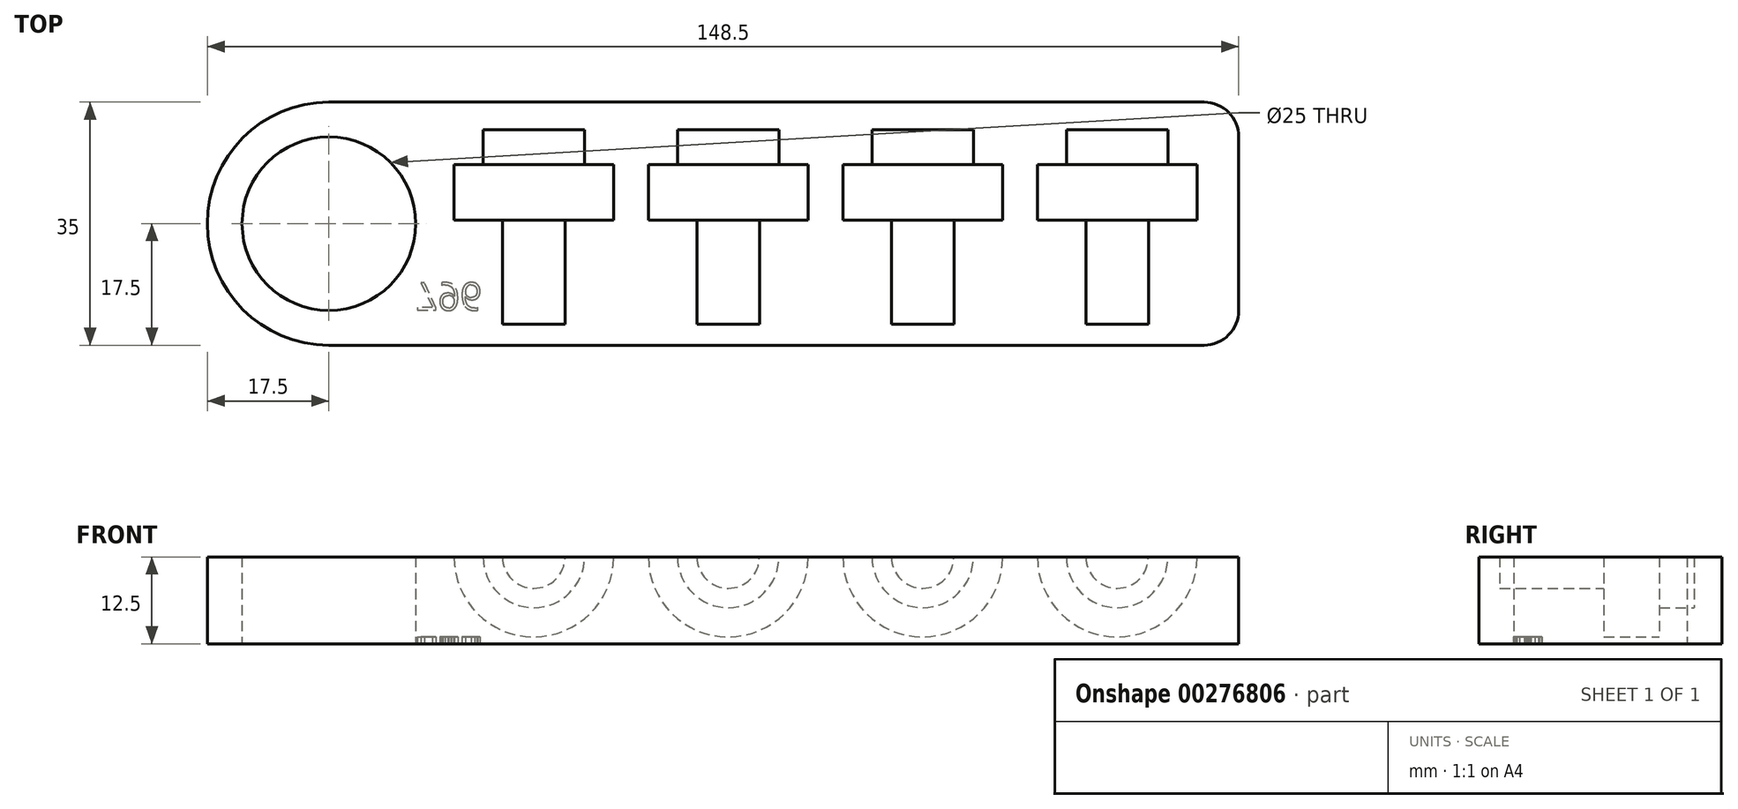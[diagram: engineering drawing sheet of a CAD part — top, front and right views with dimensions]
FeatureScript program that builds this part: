
annotation { "Feature Type Name" : "Feature", "Feature Type Description" : "" }
export const myFeature = defineFeature(function(context is Context, id is Id, definition is map)
    precondition{}
    {
        {
            var Q0;
            Q0=qCreatedBy(makeId("Top.planeOp"),FACE);
            var sketch = newSketch(context, id + "F0", { "sketchPlane" : qUnion([Q0])});
            skLineSegment(sketch, "E0.bottom", {"start": v(17.5, 0) * mm, "end": v(143.5, 0) * mm});
            skLineSegment(sketch, "E0.top", {"start": v(17.5, 35) * mm, "end": v(143.5, 35) * mm});
            skLineSegment(sketch, "E0.left", {"start": v(0, 17.5) * mm, "end": v(0, 17.5) * mm});
            skLineSegment(sketch, "E0.right", {"start": v(148.5, 5) * mm, "end": v(148.5, 30) * mm});
            skLineSegment(sketch, "E1.bottom", {"start": v(0, 0) * mm, "end": v(17.5, 0) * mm, "construction": true});
            skLineSegment(sketch, "E1.top", {"start": v(0, 17.5) * mm, "end": v(17.5, 17.5) * mm, "construction": true});
            skLineSegment(sketch, "E1.left", {"start": v(0, 0) * mm, "end": v(0, 17.5) * mm, "construction": true});
            skLineSegment(sketch, "E1.right", {"start": v(17.5, 0) * mm, "end": v(17.5, 17.5) * mm, "construction": true});
            skCircle(sketch, "E2", {"center": v(17.5, 17.5) * mm, "radius": 12.5 * mm});
            skPoint(sketch, "E3.visualSharp", {"position": v(0, 0) * mm});
            skArc(sketch, "E3.filletArc", {"start": v(0, 17.5) * mm, "mid": v(5.13, 5.13) * mm, "end": v(17.5, 0) * mm});
            skPoint(sketch, "E4.visualSharp", {"position": v(0, 35) * mm});
            skArc(sketch, "E4.filletArc", {"start": v(17.5, 35) * mm, "mid": v(5.13, 29.87) * mm, "end": v(0, 17.5) * mm});
            skPoint(sketch, "E5.visualSharp", {"position": v(148.5, 35) * mm});
            skArc(sketch, "E5.filletArc", {"start": v(148.5, 30) * mm, "mid": v(147.04, 33.54) * mm, "end": v(143.5, 35) * mm});
            skPoint(sketch, "E6.visualSharp", {"position": v(148.5, 0) * mm});
            skArc(sketch, "E6.filletArc", {"start": v(143.5, 0) * mm, "mid": v(147.04, 1.46) * mm, "end": v(148.5, 5) * mm});
            skSolve(sketch);
        }
        {
            var Q0;
            Q0=makeQuery(id+"F0.imprint","IMPRINT",FACE,{"disambiguationData":[TD([[makeQuery(id+"F0.imprint","IMPRINT",EDGE,{"derivedFrom":sQuery(id+"F0.wireOp",EDGE,"E0.bottom")}),1.0]])]});
            extrude(context, id + "F1", {"entities" : qUnion([Q0]), "depth" : 12.5 * mm, "offsetDistance" : 25 * mm});
        }
        {
            var Q0;
            Q0=makeQuery(id+"F1.opExtrude","CAP_FACE",FACE,{"disambiguationData":[OSD([sQuery(id+"F0.wireOp",EDGE,"E0.bottom"),sQuery(id+"F0.wireOp",EDGE,"E0.top"),sQuery(id+"F0.wireOp",EDGE,"E0.right"),sQuery(id+"F0.wireOp",EDGE,"E2"),sQuery(id+"F0.wireOp",EDGE,"E3.filletArc"),sQuery(id+"F0.wireOp",EDGE,"E4.filletArc"),sQuery(id+"F0.wireOp",EDGE,"E5.filletArc"),sQuery(id+"F0.wireOp",EDGE,"E6.filletArc")])],"isStart":false});
            var sketch = newSketch(context, id + "F2", { "sketchPlane" : qUnion([Q0])});
            skLineSegment(sketch, "E7.bottom", {"start": v(0, 0) * mm, "end": v(47, 0) * mm, "construction": true});
            skLineSegment(sketch, "E7.top", {"start": v(0, 3) * mm, "end": v(47, 3) * mm, "construction": true});
            skLineSegment(sketch, "E7.left", {"start": v(0, 0) * mm, "end": v(0, 3) * mm, "construction": true});
            skLineSegment(sketch, "E7.right", {"start": v(47, 0) * mm, "end": v(47, 3) * mm, "construction": true});
            skLineSegment(sketch, "E8", {"start": v(47, 3) * mm, "end": v(75, 3) * mm, "construction": true});
            skLineSegment(sketch, "E9", {"start": v(75, 3) * mm, "end": v(103, 3) * mm, "construction": true});
            skLineSegment(sketch, "E10", {"start": v(103, 3) * mm, "end": v(131, 3) * mm, "construction": true});
            skLineSegment(sketch, "E11.bottom", {"start": v(47, 3) * mm, "end": v(51.5, 3) * mm});
            skLineSegment(sketch, "E11.left", {"start": v(47, 3) * mm, "end": v(47, 18) * mm});
            skLineSegment(sketch, "E11.right", {"start": v(51.5, 3) * mm, "end": v(51.5, 18) * mm});
            skLineSegment(sketch, "E12.bottom", {"start": v(75, 3) * mm, "end": v(79.5, 3) * mm});
            skLineSegment(sketch, "E12.left", {"start": v(75, 3) * mm, "end": v(75, 18) * mm});
            skLineSegment(sketch, "E12.right", {"start": v(79.5, 3) * mm, "end": v(79.5, 18) * mm});
            skLineSegment(sketch, "E13.bottom", {"start": v(103, 3) * mm, "end": v(107.5, 3) * mm});
            skLineSegment(sketch, "E13.left", {"start": v(103, 3) * mm, "end": v(103, 18) * mm});
            skLineSegment(sketch, "E13.right", {"start": v(107.5, 3) * mm, "end": v(107.5, 18) * mm});
            skLineSegment(sketch, "E14.bottom", {"start": v(131, 3) * mm, "end": v(135.5, 3) * mm});
            skLineSegment(sketch, "E14.left", {"start": v(131, 3) * mm, "end": v(131, 18) * mm});
            skLineSegment(sketch, "E14.right", {"start": v(135.5, 3) * mm, "end": v(135.5, 18) * mm});
            skLineSegment(sketch, "E15.bottom", {"start": v(51.5, 18) * mm, "end": v(58.5, 18) * mm});
            skLineSegment(sketch, "E15.top", {"start": v(54.3, 26) * mm, "end": v(58.5, 26) * mm});
            skLineSegment(sketch, "E15.left", {"start": v(47, 18) * mm, "end": v(47, 26) * mm});
            skLineSegment(sketch, "E15.right", {"start": v(58.5, 18) * mm, "end": v(58.5, 26) * mm});
            skLineSegment(sketch, "E16.bottom", {"start": v(79.5, 18) * mm, "end": v(86.5, 18) * mm});
            skLineSegment(sketch, "E16.top", {"start": v(82.3, 26) * mm, "end": v(86.5, 26) * mm});
            skLineSegment(sketch, "E16.left", {"start": v(75, 18) * mm, "end": v(75, 26) * mm});
            skLineSegment(sketch, "E16.right", {"start": v(86.5, 18) * mm, "end": v(86.5, 26) * mm});
            skLineSegment(sketch, "E17.bottom", {"start": v(107.5, 18) * mm, "end": v(114.5, 18) * mm});
            skLineSegment(sketch, "E17.top", {"start": v(110.3, 26) * mm, "end": v(114.5, 26) * mm});
            skLineSegment(sketch, "E17.left", {"start": v(103, 18) * mm, "end": v(103, 26) * mm});
            skLineSegment(sketch, "E17.right", {"start": v(114.5, 18) * mm, "end": v(114.5, 26) * mm});
            skLineSegment(sketch, "E18.bottom", {"start": v(135.5, 18) * mm, "end": v(142.5, 18) * mm});
            skLineSegment(sketch, "E18.top", {"start": v(138.3, 26) * mm, "end": v(142.5, 26) * mm});
            skLineSegment(sketch, "E18.left", {"start": v(131, 18) * mm, "end": v(131, 26) * mm});
            skLineSegment(sketch, "E18.right", {"start": v(142.5, 18) * mm, "end": v(142.5, 26) * mm});
            skLineSegment(sketch, "E19.top", {"start": v(131, 31) * mm, "end": v(138.3, 31) * mm});
            skLineSegment(sketch, "E19.left", {"start": v(131, 26) * mm, "end": v(131, 31) * mm});
            skLineSegment(sketch, "E19.right", {"start": v(138.3, 26) * mm, "end": v(138.3, 31) * mm});
            skLineSegment(sketch, "E20.top", {"start": v(103, 31) * mm, "end": v(110.3, 31) * mm});
            skLineSegment(sketch, "E20.left", {"start": v(103, 26) * mm, "end": v(103, 31) * mm});
            skLineSegment(sketch, "E20.right", {"start": v(110.3, 26) * mm, "end": v(110.3, 31) * mm});
            skLineSegment(sketch, "E21.top", {"start": v(75, 31) * mm, "end": v(82.3, 31) * mm});
            skLineSegment(sketch, "E21.left", {"start": v(75, 26) * mm, "end": v(75, 31) * mm});
            skLineSegment(sketch, "E21.right", {"start": v(82.3, 26) * mm, "end": v(82.3, 31) * mm});
            skLineSegment(sketch, "E22.top", {"start": v(47, 31) * mm, "end": v(54.3, 31) * mm});
            skLineSegment(sketch, "E22.left", {"start": v(47, 26) * mm, "end": v(47, 31) * mm});
            skLineSegment(sketch, "E22.right", {"start": v(54.3, 26) * mm, "end": v(54.3, 31) * mm});
            skSolve(sketch);
        }
        {
            var Q0;
            Q0=makeQuery(id+"F2.imprint","IMPRINT",FACE,{"disambiguationData":[TD([[makeQuery(id+"F2.imprint","IMPRINT",EDGE,{"derivedFrom":sQuery(id+"F2.wireOp",EDGE,"E11.bottom")}),1.0]])]});
            var Q1;
            Q1=sQuery(id+"F2.wireOp",EDGE,"E11.left");
            revolve(context, id + "F3", {"operationType" : NewBodyOperationType.REMOVE, "entities" : qUnion([Q0]), "axis" : qUnion([Q1]), "revolveType" : RevolveType.FULL, "oppositeDirection" : true});
        }
        {
            var Q0;
            Q0=makeQuery(id+"F2.imprint","IMPRINT",FACE,{"disambiguationData":[TD([[makeQuery(id+"F2.imprint","IMPRINT",EDGE,{"derivedFrom":sQuery(id+"F2.wireOp",EDGE,"E12.bottom")}),1.0]])]});
            var Q1;
            Q1=sQuery(id+"F2.wireOp",EDGE,"E16.left");
            revolve(context, id + "F4", {"operationType" : NewBodyOperationType.REMOVE, "entities" : qUnion([Q0]), "axis" : qUnion([Q1]), "revolveType" : RevolveType.FULL, "oppositeDirection" : true});
        }
        {
            var Q0;
            Q0=makeQuery(id+"F2.imprint","IMPRINT",FACE,{"disambiguationData":[TD([[makeQuery(id+"F2.imprint","IMPRINT",EDGE,{"derivedFrom":sQuery(id+"F2.wireOp",EDGE,"E13.bottom")}),1.0]])]});
            var Q1;
            Q1=sQuery(id+"F2.wireOp",EDGE,"E17.left");
            revolve(context, id + "F5", {"operationType" : NewBodyOperationType.REMOVE, "entities" : qUnion([Q0]), "axis" : qUnion([Q1]), "revolveType" : RevolveType.FULL, "oppositeDirection" : true});
        }
        {
            var Q0;
            Q0=makeQuery(id+"F2.imprint","IMPRINT",FACE,{"disambiguationData":[TD([[makeQuery(id+"F2.imprint","IMPRINT",EDGE,{"derivedFrom":sQuery(id+"F2.wireOp",EDGE,"E14.bottom")}),1.0]])]});
            var Q1;
            Q1=sQuery(id+"F2.wireOp",EDGE,"E18.left");
            revolve(context, id + "F6", {"operationType" : NewBodyOperationType.REMOVE, "entities" : qUnion([Q0]), "axis" : qUnion([Q1]), "revolveType" : RevolveType.FULL, "oppositeDirection" : true});
        }
        {
            var Q0;
            Q0=makeQuery(id+"F1.opExtrude","CAP_FACE",FACE,{"disambiguationData":[OSD([sQuery(id+"F0.wireOp",EDGE,"E0.bottom"),sQuery(id+"F0.wireOp",EDGE,"E0.top"),sQuery(id+"F0.wireOp",EDGE,"E0.right"),sQuery(id+"F0.wireOp",EDGE,"E2"),sQuery(id+"F0.wireOp",EDGE,"E3.filletArc"),sQuery(id+"F0.wireOp",EDGE,"E4.filletArc"),sQuery(id+"F0.wireOp",EDGE,"E5.filletArc"),sQuery(id+"F0.wireOp",EDGE,"E6.filletArc")])],"isStart":true});
            var sketch = newSketch(context, id + "F7", { "sketchPlane" : qUnion([Q0])});
            skLineSegment(sketch, "E23.bottom", {"start": v(0, 0) * mm, "end": v(30, 0) * mm, "construction": true});
            skLineSegment(sketch, "E23.top", {"start": v(0, -5) * mm, "end": v(30, -5) * mm, "construction": true});
            skLineSegment(sketch, "E23.left", {"start": v(0, 0) * mm, "end": v(0, -5) * mm, "construction": true});
            skLineSegment(sketch, "E23.right", {"start": v(30, 0) * mm, "end": v(30, -5) * mm, "construction": true});
            skText(sketch, "E24", { "text": "796", "fontName": "OpenSans-Regular.ttf"});
            const initialGuessF7  = {"E24": [0.03, -0.009, 1, 0, 0.004]};
            skSetInitialGuess(sketch, initialGuessF7);
            skSolve(sketch);
        }
        {
            var Q0;
            Q0 = qSketchRegion(id + "F7", true);
            extrude(context, id + "F8", {"entities" : qUnion([Q0]), "operationType" : NewBodyOperationType.REMOVE, "oppositeDirection" : true, "depth" : 1 * mm});
        }
    });
